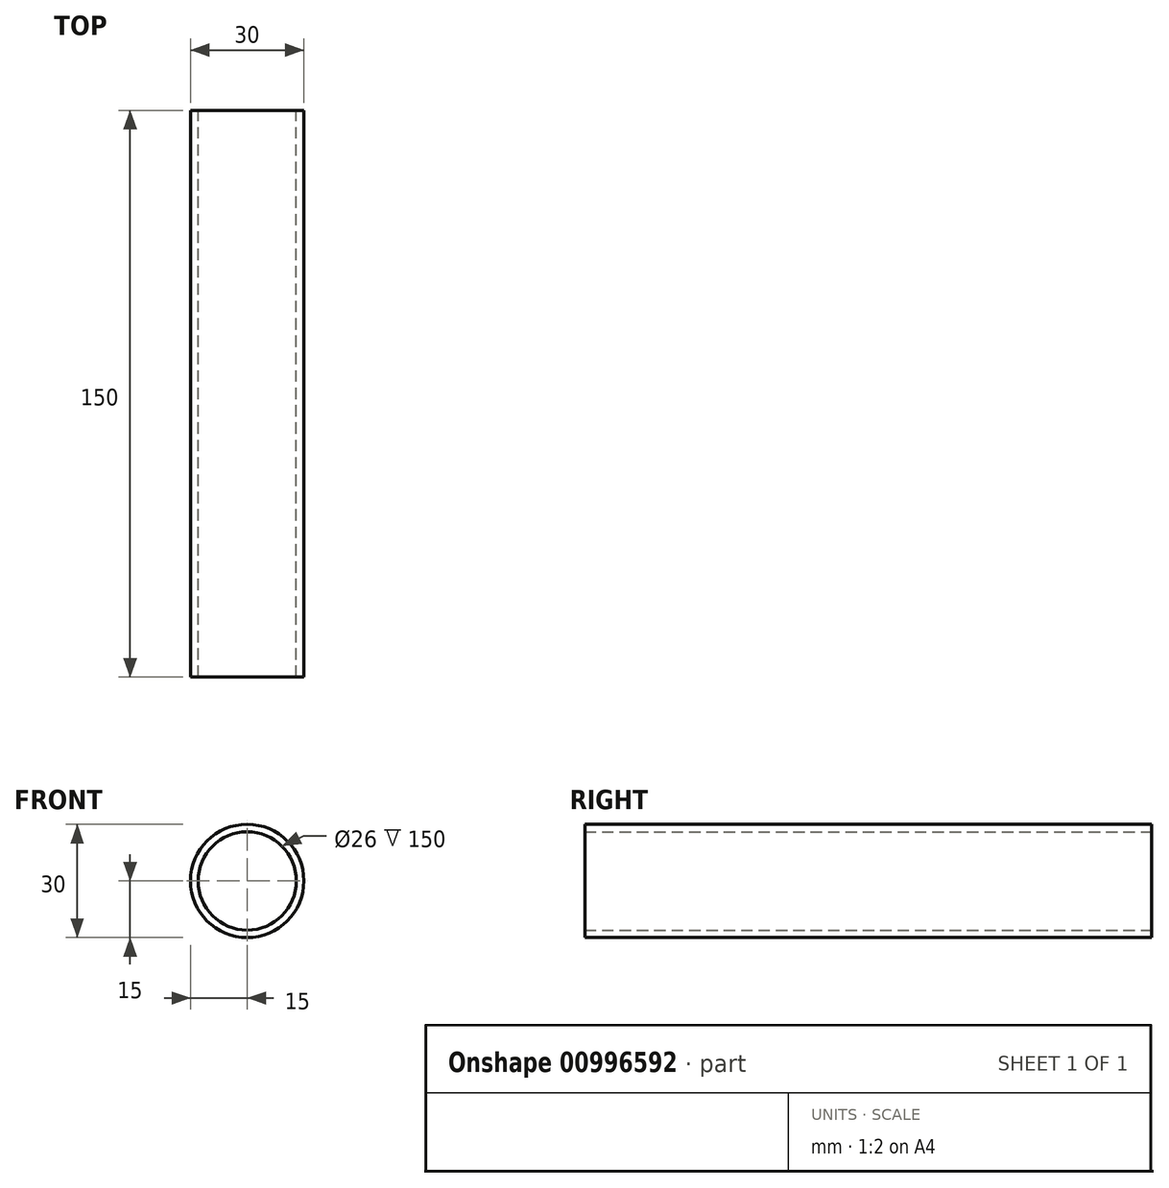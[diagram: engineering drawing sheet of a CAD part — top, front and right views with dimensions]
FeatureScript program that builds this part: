
annotation { "Feature Type Name" : "Feature", "Feature Type Description" : "" }
export const myFeature = defineFeature(function(context is Context, id is Id, definition is map)
    precondition{}
    {
        {
            var Q0;
            Q0=qCreatedBy(makeId("Front.planeOp"),FACE);
            var sketch = newSketch(context, id + "F0", { "sketchPlane" : qUnion([Q0])});
            skCircle(sketch, "E0", {"center": v(0, 0) * mm, "radius": 15 * mm});
            skCircle(sketch, "E1", {"center": v(0, 0) * mm, "radius": 13 * mm});
            skSolve(sketch);
        }
        {
            var Q0;
            Q0=makeQuery(id+"F0.imprint","IMPRINT",FACE,{"disambiguationData":[TD([[makeQuery(id+"F0.imprint","IMPRINT",EDGE,{"derivedFrom":sQuery(id+"F0.wireOp",EDGE,"E0")}),1.0]])]});
            extrude(context, id + "F1", {"entities" : qUnion([Q0]), "depth" : 150 * mm, "offsetDistance" : 25 * mm});
        }
    });
